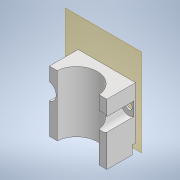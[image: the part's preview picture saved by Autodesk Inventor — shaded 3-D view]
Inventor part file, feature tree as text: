
AUTODESK INVENTOR PART (.ipt)
format: ipt  version: 2020.2 (Build 242310000, 310)  size: 172,544 bytes
history: native  units: mm
features: reference x6, sketch x5, extrude x5, other x4, plane x3, projected_geometry x1
ambient origin geometry x8: Origin, YZ Plane, XZ Plane, XY Plane, X Axis, Y Axis, Z Axis, Center Point
bodies: Solid1 (feature_tree)
feature tree (24):
  sketch  "Sketch1"  dims[d0=0.4mm d1=10.0mm d2=0.0mm]
  plane  "Work Plane1"
  extrude  "Extrusion1"  Depth=10.0mm TaperAngle=0.0deg
  extrude  "Extrusion2"  Depth=34.0mm
  extrude  "Extrusion3"  Depth=24.0mm
  plane  "Work Plane2"
  plane  "Work Plane3"
  extrude  "Extrusion4"  Depth=36.0mm
  extrude  "Extrusion5"  Depth=3.0mm
  reference  "Reference1"
  sketch  "Sketch2"  dims[d10=17.0mm d11=0.0mm d12=34.0mm]
  reference  "Reference2"
  reference  "Reference3"
  projected_geometry  "Projected Loop1"
  sketch  "Sketch4"  dims[d13=4.5mm d14=24.0mm]
  reference  "Reference4"
  sketch  "Sketch5"  dims[d15=5.0mm d16=36.0mm]
  reference  "Reference5"
  reference  "Reference6"
  sketch  "Sketch6"  dims[d17=3.0mm d18=3.0mm d19=0.4mm d20=10.0mm d21=0.0mm d22=14.0mm d23=7.0mm d24=3.64985mm d25=1.0mm d26=0.0mm d27=4.0mm d28=0.0mm]
  other  "<userpath>\OneDrive\Apps\0011_VentControlValve\Drawings\Assembly.iam"
  other  "Assembly.iam"
  other  "center Section:1"
  other  "motor+Gearbox:1"
